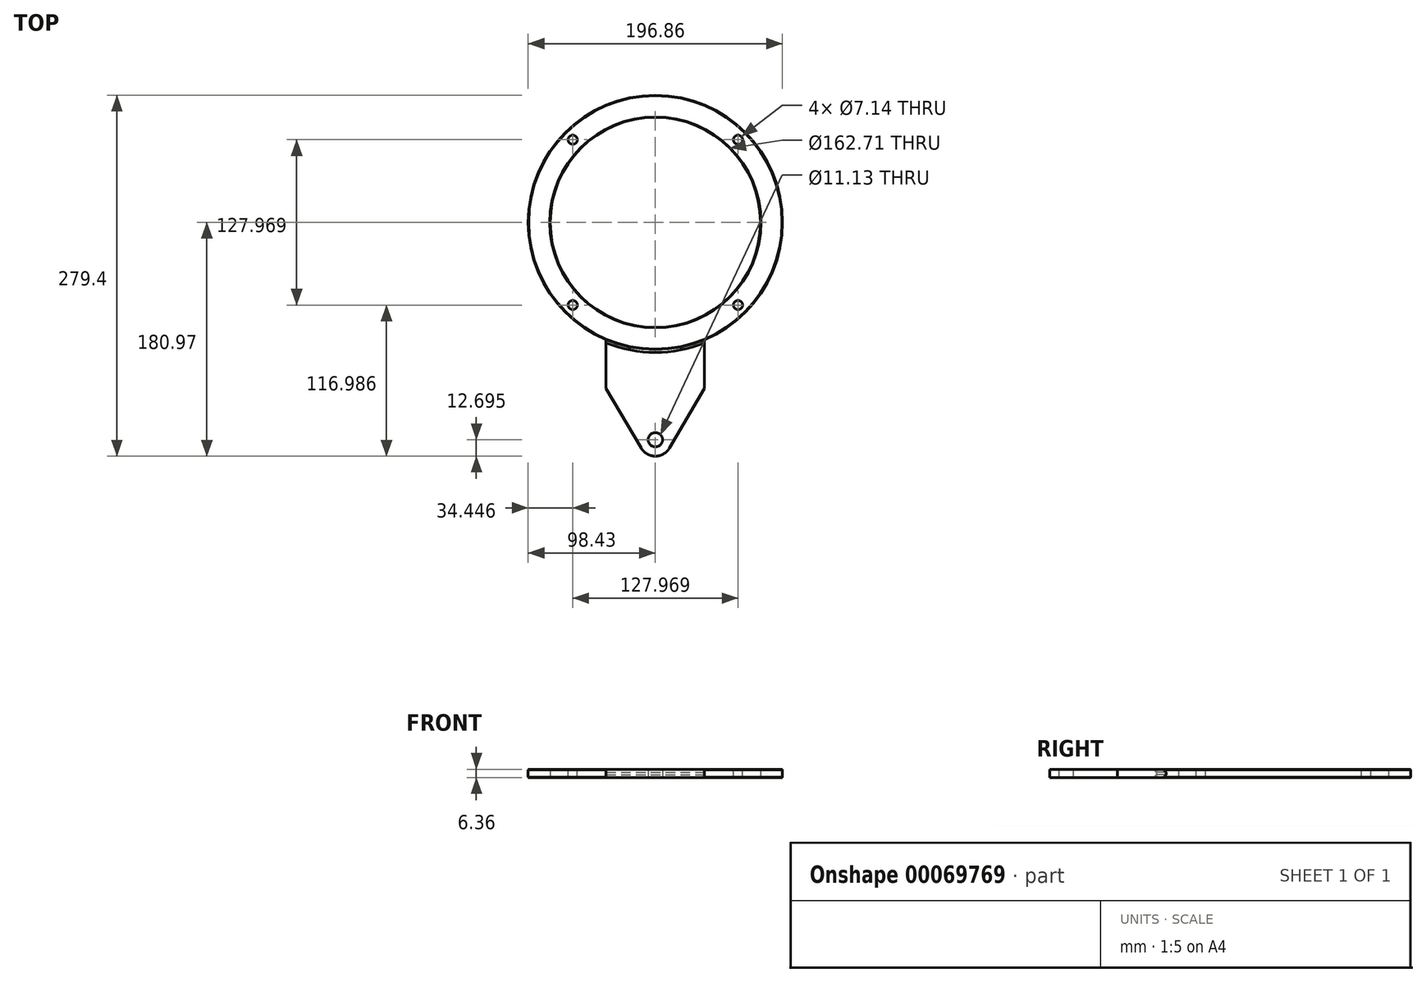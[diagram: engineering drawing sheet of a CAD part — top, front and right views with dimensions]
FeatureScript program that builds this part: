
annotation { "Feature Type Name" : "Feature", "Feature Type Description" : "" }
export const myFeature = defineFeature(function(context is Context, id is Id, definition is map)
    precondition{}
    {
        {
            var Q0;
            Q0=qCreatedBy(makeId("Top.planeOp"),FACE);
            var sketch = newSketch(context, id + "F0", { "sketchPlane" : qUnion([Q0])});
            skArc(sketch, "E0", {"start": v(-38.1, -90.75) * mm, "mid": v(0, -98.43) * mm, "end": v(38.1, -90.75) * mm});
            skCircle(sketch, "E1", {"center": v(0, -168.28) * mm, "radius": 5.56 * mm});
            skArc(sketch, "E2", {"start": v(-10.94, -174.72) * mm, "mid": v(0, -180.98) * mm, "end": v(10.94, -174.72) * mm});
            skLineSegment(sketch, "E3", {"start": v(38.1, -90.75) * mm, "end": v(38.1, -128.59) * mm});
            skLineSegment(sketch, "E4", {"start": v(0, -98.43) * mm, "end": v(38.1, -98.43) * mm, "construction": true});
            skLineSegment(sketch, "E5", {"start": v(38.1, -128.59) * mm, "end": v(10.94, -174.72) * mm});
            skLineSegment(sketch, "E6.MirrorCS", {"start": v(-38.1, -128.59) * mm, "end": v(-10.94, -174.72) * mm});
            skPoint(sketch, "E7.orphan", {"position": v(7.3, -180.92) * mm});
            skPoint(sketch, "E8.orphan", {"position": v(-7.3, -180.92) * mm});
            skLineSegment(sketch, "E9", {"start": v(0, -98.43) * mm, "end": v(0, 0) * mm, "construction": true});
            skLineSegment(sketch, "E10.MirrorCS", {"start": v(-38.1, -90.75) * mm, "end": v(-38.1, -128.59) * mm});
            skSolve(sketch);
        }
        {
            var Q0;
            Q0 = qSketchRegion(id + "F0", true);
            extrude(context, id + "F1", {"entities" : qUnion([Q0]), "endBound" : BoundingType.SYMMETRIC, "depth" : 6.35 * mm});
        }
        {
            var Q0;
            Q0=qCreatedBy(makeId("Top.planeOp"),FACE);
            var sketch = newSketch(context, id + "F2", { "sketchPlane" : qUnion([Q0])});
            skCircle(sketch, "E11", {"center": v(0, 0) * mm, "radius": 98.43 * mm});
            skCircle(sketch, "E12", {"center": v(0, 0) * mm, "radius": 81.36 * mm});
            skSolve(sketch);
        }
        {
            var Q0;
            Q0 = qSketchRegion(id + "F2", true);
            extrude(context, id + "F3", {"entities" : qUnion([Q0]), "endBound" : BoundingType.SYMMETRIC, "depth" : 6.35 * mm});
        }
        {
            var Q0;
            Q0=makeQuery(id+"F3.opExtrude","CAP_EDGE",EDGE,{"disambiguationData":[OSD([sQuery(id+"F2.wireOp",EDGE,"E11")])],"isStart":false});
            var Q1;
            Q1=makeQuery(id+"F3.opExtrude","CAP_EDGE",EDGE,{"disambiguationData":[OSD([sQuery(id+"F2.wireOp",EDGE,"E12")])],"isStart":false});
            var Q2;
            Q2=makeQuery(id+"F3.opExtrude","CAP_EDGE",EDGE,{"disambiguationData":[OSD([sQuery(id+"F2.wireOp",EDGE,"E12")])],"isStart":true});
            var Q3;
            Q3=makeQuery(id+"F3.opExtrude","CAP_EDGE",EDGE,{"disambiguationData":[OSD([sQuery(id+"F2.wireOp",EDGE,"E11")])],"isStart":true});
            chamfer(context, id + "F4", {"entities" : qUnion([Q0, Q1, Q2, Q3]), "width" : 0.38 * mm, "tangentPropagation" : true});
        }
        {
            var Q0;
            Q0=makeQuery(id+"F1.opExtrude","CAP_EDGE",EDGE,{"disambiguationData":[OSD([sQuery(id+"F0.wireOp",EDGE,"E0")])],"isStart":false});
            var Q1;
            Q1=makeQuery(id+"F1.opExtrude","CAP_EDGE",EDGE,{"disambiguationData":[OSD([sQuery(id+"F0.wireOp",EDGE,"E0")])],"isStart":true});
            chamfer(context, id + "F5", {"entities" : qUnion([Q0, Q1]), "width" : 2.3 * mm, "tangentPropagation" : true});
        }
        {
            var Q0;
            Q0=makeQuery(id+"F3.opExtrude","CAP_FACE",FACE,{"disambiguationData":[OSD([sQuery(id+"F2.wireOp",EDGE,"E11"),sQuery(id+"F2.wireOp",EDGE,"E12")])],"isStart":false});
            var sketch = newSketch(context, id + "F6", { "sketchPlane" : qUnion([Q0])});
            skCircle(sketch, "E13", {"center": v(0, 0) * mm, "radius": 90.49 * mm, "construction": true});
            skLineSegment(sketch, "E14", {"start": v(0, 0) * mm, "end": v(0, -90.49) * mm, "construction": true});
            skLineSegment(sketch, "E15", {"start": v(0, 0) * mm, "end": v(-63.98, -63.98) * mm, "construction": true});
            skLineSegment(sketch, "E16", {"start": v(0, 0) * mm, "end": v(63.98, 63.98) * mm, "construction": true});
            skLineSegment(sketch, "E17", {"start": v(0, 0) * mm, "end": v(-63.98, 63.98) * mm, "construction": true});
            skLineSegment(sketch, "E18", {"start": v(0, 0) * mm, "end": v(63.98, -63.98) * mm, "construction": true});
            skSolve(sketch);
        }
        {
            var Q0;
            Q0=sQuery(id+"F6.wireOp",VERTEX,"E15.end");
            var Q1;
            Q1=sQuery(id+"F6.wireOp",VERTEX,"E17.end");
            var Q2;
            Q2=sQuery(id+"F6.wireOp",VERTEX,"E16.end");
            var Q3;
            Q3=sQuery(id+"F6.wireOp",VERTEX,"E18.end");
            var Q4;
            Q4=makeQuery(id+"F3.opExtrude","SWEPT_BODY",BODY,{"disambiguationData":[OSD([sQuery(id+"F2.wireOp",EDGE,"E11"),sQuery(id+"F2.wireOp",EDGE,"E12")])]});
            hole(context, id + "F7", {"style" : HoleStyle.SIMPLE, "holeDiameter" : 7.14 * mm, "endStyle" : HoleEndStyle.THROUGH, "locations" : qUnion([Q0, Q1, Q2, Q3]), "scope" : qUnion([Q4])});
        }
    });
